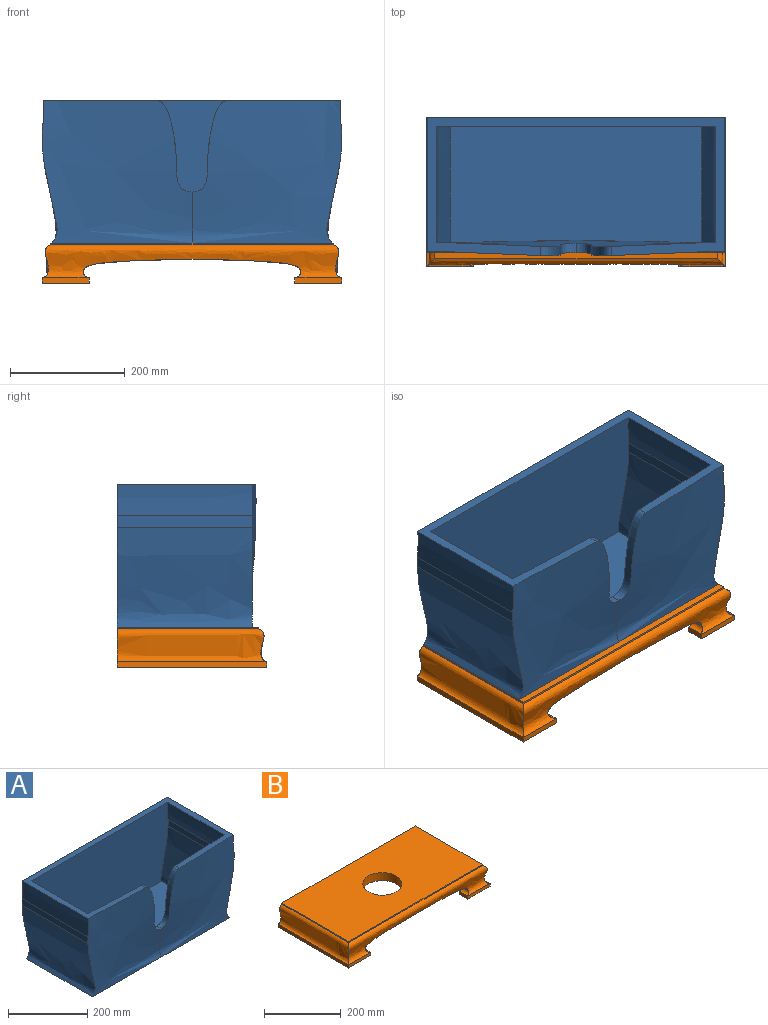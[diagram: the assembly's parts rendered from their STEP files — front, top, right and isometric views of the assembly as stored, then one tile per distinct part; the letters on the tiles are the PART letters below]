
ASSEMBLY  parts=2 mates=1
PART A: 23 faces, bbox 552.5x273.9x281.9 mm
  f0: plane 519.96x243.29mm, normal (0,0,1), area 20949.6mm2, adj f1,f2,f3,f7,f8,f9,f12,f16
  f1: bspline ~260.35x250.13mm, area 57316.3mm2, adj f0,f4,f5,f7,f8,f11,f21
  f2: offset ~295.54x281.88mm, area 49889.1mm2, adj f0,f13,f14,f16,f17,f20,f21
  f3: plane 520.7x247.65mm, normal (0,1,0), area 124208.6mm2, adj f0,f4,f5,f6,f8,f9,f10,f11
  f4: plane 488.95x234.95mm, normal (0,0,-1), area 114878.8mm2, adj f1,f3,f7,f10,f11
  f5: plane 234.95x20.14mm, normal (1,0,0), area 4732.9mm2, adj f1,f3,f8,f11
  f6: plane 234.95x20.14mm, normal (-1,0,0), area 4732.9mm2, adj f3,f7,f9,f10
  f7: bspline ~263.79x250.13mm, area 57318.7mm2, adj f0,f1,f4,f6,f9,f10,f22
  f8: extruded ~234.95x54.33mm, area 12792.8mm2, adj f0,f1,f3,f5
  f9: extruded ~234.95x54.33mm, area 12792.8mm2, adj f0,f3,f6,f7
  f10: extruded ~234.95x173.18mm, area 41869.2mm2, adj f3,f4,f6,f7
  f11: extruded ~234.95x173.18mm, area 41869.2mm2, adj f1,f3,f4,f5
  f12: plane 500.1x242.92mm, normal (0,-1,0), area 109180.9mm2, adj f0,f13,f14,f15,f17,f18,f19,f20
  f13: plane 442x206.03mm, normal (0,0,1), area 87957mm2, adj f2,f12,f16,f19,f20
  f14: plane 202.57x19.44mm, normal (-1,0,0), area 3925.3mm2, adj f2,f12,f17,f20
  f15: plane 202.57x19.44mm, normal (1,0,0), area 3925.3mm2, adj f12,f16,f18,f19
  f16: offset ~295.54x281.88mm, area 49890.4mm2, adj f0,f2,f13,f15,f18,f19,f22
  f17: extruded ~202.4x54.75mm, area 11091.5mm2, adj f0,f2,f12,f14
  f18: extruded ~202.4x54.75mm, area 11091.5mm2, adj f0,f12,f15,f16
  f19: extruded ~202.82x157.64mm, area 32454.6mm2, adj f12,f13,f15,f16
  f20: extruded ~202.82x157.64mm, area 32454.6mm2, adj f2,f12,f13,f14
  f21: extruded ~158.75x60.92mm, area 2939mm2, adj f0,f1,f2,f22
  f22: extruded ~158.75x60.92mm, area 2939mm2, adj f0,f7,f16,f21
PART B: 36 faces, bbox 520.7x260.4x69.9 mm
  f0: plane 260.35x81.53mm, normal (0,0,-1), area 10795.1mm2, adj f7,f10,f18,f19,f27,f30,f31,f32
  f1: plane 260.35x81.53mm, normal (0,0,-1), area 10795.1mm2, adj f8,f16,f17,f19,f28,f30,f31,f33
  f2: extruded ~22.88x2.72mm, area 62.6mm2, adj f3,f9,f21,f30
  f3: extruded ~189.29x24.23mm, area 4562.2mm2, adj f2,f4,f21,f30
  f4: extruded ~189.29x24.23mm, area 4562.2mm2, adj f3,f5,f21,f30
  f5: extruded ~22.88x2.72mm, area 62.6mm2, adj f4,f6,f21,f30
  f6: extruded ~31.75x9.91mm, area 346.6mm2, adj f5,f7,f21,f30
  f7: plane 31.75x9.53mm, normal (1,0,0), area 302.4mm2, adj f0,f6,f10,f30
  f8: plane 31.75x9.53mm, normal (-1,0,0), area 302.4mm2, adj f1,f9,f16,f30
  f9: extruded ~31.75x9.91mm, area 346.6mm2, adj f2,f8,f21,f30
  f10: plane 81.53x9.53mm, normal (0,-1,0), area 776.6mm2, adj f0,f7,f18,f21
  f11: extruded ~260.35x57.08mm, area 16945mm2, adj f15,f17,f19,f21
  f12: extruded ~260.35x57.08mm, area 16945mm2, adj f13,f18,f19,f21
  f13: plane 246.09x3.25mm, normal (-1,0,0), area 799.3mm2, adj f12,f14,f19,f20
  f14: plane 492.19x246.09mm, normal (0,0,1), area 113017.4mm2, adj f13,f15,f19,f20,f35
  f15: plane 246.09x3.25mm, normal (1,0,0), area 799.3mm2, adj f11,f14,f19,f20
  f16: plane 81.53x9.53mm, normal (0,-1,0), area 776.6mm2, adj f1,f8,f17,f21
  f17: plane 260.35x9.53mm, normal (1,0,0), area 2479.8mm2, adj f1,f11,f16,f19
  f18: plane 260.35x9.53mm, normal (-1,0,0), area 2479.8mm2, adj f0,f10,f12,f19
  f19: plane 520.7x69.85mm, normal (0,1,0), area 21111mm2, adj f0,f1,f11,f12,f13,f14,f15,f17
  f20: plane 492.19x3.25mm, normal (0,-1,0), area 1598.5mm2, adj f13,f14,f15,f21
  f21: extruded ~520.7x57.08mm, area 21097.4mm2, adj f2,f3,f4,f5,f6,f9,f10,f11
  f22: extruded ~19.05x2.72mm, area 53.3mm2, adj f19,f23,f29,f31
  f23: extruded ~189.29x22.7mm, area 3736.2mm2, adj f19,f22,f24,f31
  f24: extruded ~189.29x22.7mm, area 3736.2mm2, adj f19,f23,f25,f31
  f25: extruded ~19.05x2.72mm, area 53.3mm2, adj f19,f24,f26,f31
  f26: extruded ~19.05x9.91mm, area 245.2mm2, adj f19,f25,f27,f31
  f27: plane 19.05x9.53mm, normal (1,0,0), area 181.5mm2, adj f0,f19,f26,f31
  f28: plane 19.05x9.53mm, normal (-1,0,0), area 181.5mm2, adj f1,f19,f29,f31
  f29: extruded ~19.05x9.91mm, area 245.2mm2, adj f19,f22,f28,f31
  f30: plane 457.2x44.45mm, normal (0,1,0), area 6057.6mm2, adj f0,f1,f2,f3,f4,f5,f6,f7
  f31: plane 457.2x44.45mm, normal (0,-1,0), area 6057.6mm2, adj f0,f1,f22,f23,f24,f25,f26,f27
  f32: plane 209.55x44.45mm, normal (1,0,0), area 9314.5mm2, adj f0,f30,f31,f34
  f33: plane 209.55x44.45mm, normal (-1,0,0), area 9314.5mm2, adj f1,f30,f31,f34
  f34: plane 457.2x209.55mm, normal (0,0,-1), area 87698.9mm2, adj f30,f31,f32,f33,f35
  f35: cylinder r=50.8mm len=101.6mm, axis (0,0,-1), area 8107.3mm2, adj f14,f34
PLACE A t=(-332.07,97.82,-52.17)mm
PLACE B t=(-332.07,97.82,-299.82)mm
MATE fastened B.f14 <-> A.f4  axis (0,0,1) through (-71.72,97.82,-299.82)mm
